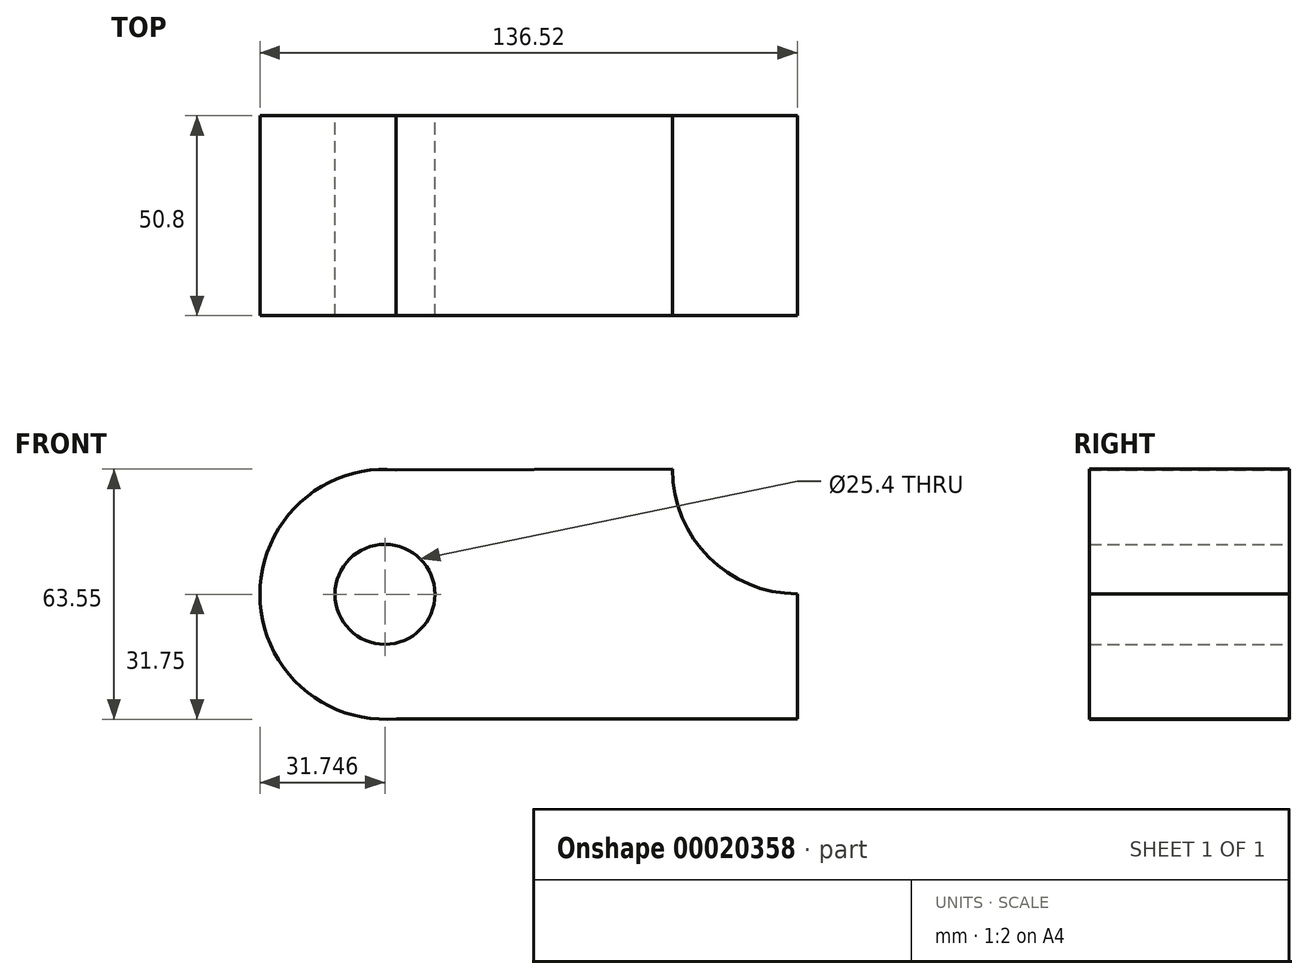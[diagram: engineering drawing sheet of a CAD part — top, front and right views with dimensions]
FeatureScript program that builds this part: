
annotation { "Feature Type Name" : "Feature", "Feature Type Description" : "" }
export const myFeature = defineFeature(function(context is Context, id is Id, definition is map)
    precondition{}
    {
        {
            var Q0;
            Q0=qCreatedBy(makeId("Front.planeOp"),FACE);
            var sketch = newSketch(context, id + "F0", { "sketchPlane" : qUnion([Q0])});
            skLineSegment(sketch, "E0", {"start": v(-58.21, 28.67) * mm, "end": v(-58.21, -34.57) * mm});
            skLineSegment(sketch, "E1", {"start": v(-58.21, -34.57) * mm, "end": v(46.56, -34.57) * mm});
            skLineSegment(sketch, "E2", {"start": v(46.56, -34.57) * mm, "end": v(46.56, 28.93) * mm});
            skLineSegment(sketch, "E3", {"start": v(46.56, 28.93) * mm, "end": v(-58.21, 28.67) * mm});
            skCircle(sketch, "E4", {"center": v(-58.21, -2.95) * mm, "radius": 31.75 * mm});
            skCircle(sketch, "E5", {"center": v(-58.21, -2.95) * mm, "radius": 12.7 * mm});
            skLineSegment(sketch, "E6", {"start": v(46.56, 28.93) * mm, "end": v(14.81, 28.85) * mm});
            skCircle(sketch, "E7", {"center": v(46.56, 28.93) * mm, "radius": 31.77 * mm});
            skSolve(sketch);
        }
        {
            var Q0;
            {var subQ1=sQuery(id+"F0.wireOp",EDGE,"E0");var subQ5=sQuery(id+"F0.wireOp",EDGE,"E3");var subQ9=makeQuery(id+"F0.imprint","INTERSECT",VERTEX,{"derivedFrom":[subQ1,subQ5]});Q0=makeQuery(id+"F0.imprint","IMPRINT",FACE,{"disambiguationData":[TD([[makeQuery(id+"F0.imprint","IMPRINT",EDGE,{"disambiguationData":[TD([[subQ9,-1.0]])],"derivedFrom":subQ1}),1.0]])]});}
            var Q1;
            {var subQ1=sQuery(id+"F0.wireOp",EDGE,"E3");var subQ5=sQuery(id+"F0.wireOp",EDGE,"E0");var subQ6=makeQuery(id+"F0.imprint","INTERSECT",VERTEX,{"derivedFrom":[subQ5,subQ1]});Q1=makeQuery(id+"F0.imprint","IMPRINT",FACE,{"disambiguationData":[TD([[makeQuery(id+"F0.imprint","IMPRINT",EDGE,{"disambiguationData":[TD([[subQ6,-1.0]])],"derivedFrom":subQ5}),-1.0]])]});}
            var Q2;
            {var subQ3=sQuery(id+"F0.wireOp",EDGE,"E1");var subQ7=sQuery(id+"F0.wireOp",EDGE,"E2");var subQ9=makeQuery(id+"F0.imprint","INTERSECT",VERTEX,{"derivedFrom":[subQ3,subQ7]});Q2=makeQuery(id+"F0.imprint","IMPRINT",FACE,{"disambiguationData":[TD([[makeQuery(id+"F0.imprint","IMPRINT",EDGE,{"disambiguationData":[TD([[subQ9,1.0]])],"derivedFrom":subQ3}),1.0]])]});}
            extrude(context, id + "F1", {"entities" : qUnion([Q0, Q1, Q2]), "depth" : 50.8 * mm});
        }
    });
